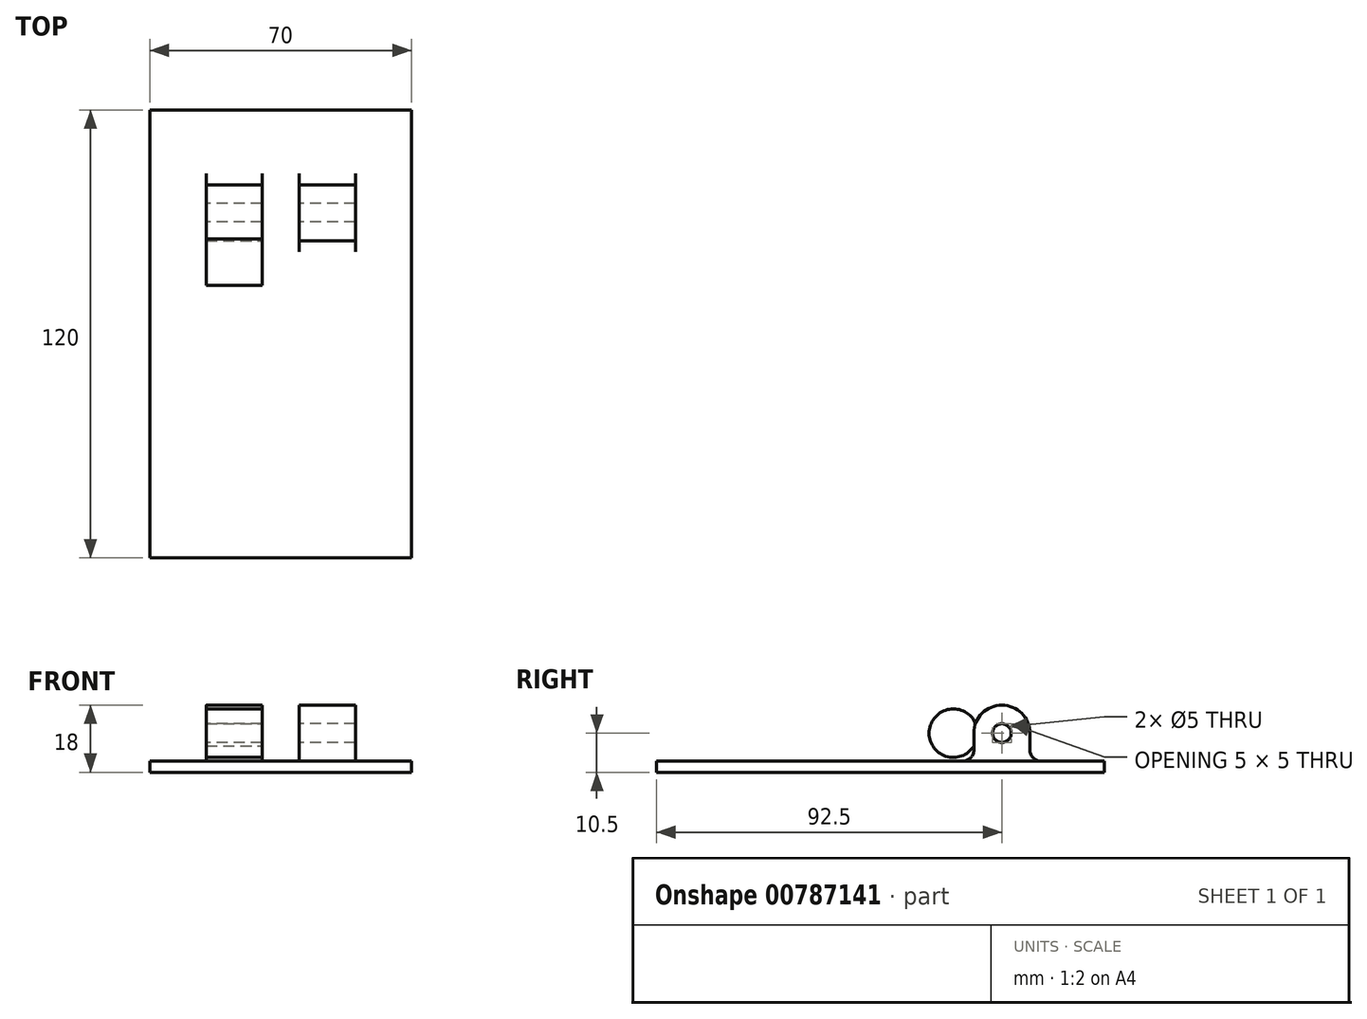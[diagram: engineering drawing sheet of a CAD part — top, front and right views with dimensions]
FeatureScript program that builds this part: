
annotation { "Feature Type Name" : "Feature", "Feature Type Description" : "" }
export const myFeature = defineFeature(function(context is Context, id is Id, definition is map)
    precondition{}
    {
        {
            var Q0;
            Q0=qCreatedBy(makeId("Right.planeOp"),FACE);
            var sketch = newSketch(context, id + "F0", { "sketchPlane" : qUnion([Q0])});
            skLineSegment(sketch, "E0.bottom", {"start": v(0, 0) * mm, "end": v(120, 0) * mm});
            skLineSegment(sketch, "E0.top", {"start": v(0, -3) * mm, "end": v(120, -3) * mm});
            skLineSegment(sketch, "E0.left", {"start": v(0, 0) * mm, "end": v(0, -3) * mm});
            skLineSegment(sketch, "E0.right", {"start": v(120, 0) * mm, "end": v(120, -3) * mm});
            skLineSegment(sketch, "E1.bottom", {"start": v(85, 0) * mm, "end": v(100, 0) * mm});
            skLineSegment(sketch, "E1.top", {"start": v(85, 15) * mm, "end": v(100, 15) * mm});
            skLineSegment(sketch, "E1.left", {"start": v(85, 0) * mm, "end": v(85, 15) * mm});
            skLineSegment(sketch, "E1.right", {"start": v(100, 0) * mm, "end": v(100, 15) * mm});
            skLineSegment(sketch, "E2", {"start": v(85, 15) * mm, "end": v(100, 0) * mm, "construction": true});
            skPoint(sketch, "E3", {"position": v(92.5, 7.5) * mm});
            skSolve(sketch);
        }
        {
            var Q0;
            Q0=makeQuery(id+"F0.imprint","IMPRINT",FACE,{"disambiguationData":[TD([[makeQuery(id+"F0.imprint","IMPRINT",EDGE,{"derivedFrom":sQuery(id+"F0.wireOp",EDGE,"E1.top")}),-1.0]])]});
            var Q1;
            Q1=makeQuery(id+"F0.imprint","IMPRINT",FACE,{"disambiguationData":[TD([[makeQuery(id+"F0.imprint","IMPRINT",EDGE,{"derivedFrom":sQuery(id+"F0.wireOp",EDGE,"E0.top")}),1.0]])]});
            extrude(context, id + "F1", {"entities" : qUnion([Q0, Q1]), "depth" : 70 * mm, "offsetDistance" : 25 * mm});
        }
        {
            var Q0;
            Q0=sQuery(id+"F0.wireOp",VERTEX,"E3");
            var Q1;
            Q1=makeQuery(id+"F1.opExtrude","SWEPT_BODY",BODY,{"disambiguationData":[OSD([sQuery(id+"F0.wireOp",EDGE,"E0.bottom"),sQuery(id+"F0.wireOp",EDGE,"E0.top"),sQuery(id+"F0.wireOp",EDGE,"E0.left"),sQuery(id+"F0.wireOp",EDGE,"E0.right"),sQuery(id+"F0.wireOp",EDGE,"E1.top"),sQuery(id+"F0.wireOp",EDGE,"E1.left"),sQuery(id+"F0.wireOp",EDGE,"E1.right")])]});
            hole(context, id + "F2", {"style" : HoleStyle.SIMPLE, "endStyle" : HoleEndStyle.THROUGH, "oppositeDirection" : true, "holeDiameter" : 5 * mm, "majorDiameter" : 5 * mm, "isTappedThrough" : true, "tappedDepth" : 12 * mm, "tapClearance" : 3, "locations" : qUnion([Q0]), "scope" : qUnion([Q1])});
        }
        {
            var Q0;
            Q0=makeQuery(id+"F1.opExtrude","SWEPT_FACE",FACE,{"disambiguationData":[OSD([sQuery(id+"F0.wireOp",EDGE,"E1.right")])]});
            var sketch = newSketch(context, id + "F3", { "sketchPlane" : qUnion([Q0])});
            skLineSegment(sketch, "E4.bottom", {"start": v(-70, 15) * mm, "end": v(-55, 15) * mm});
            skLineSegment(sketch, "E4.top", {"start": v(-70, 0) * mm, "end": v(-55, 0) * mm});
            skLineSegment(sketch, "E4.left", {"start": v(-70, 15) * mm, "end": v(-70, 0) * mm});
            skLineSegment(sketch, "E4.right", {"start": v(-55, 15) * mm, "end": v(-55, 0) * mm});
            skLineSegment(sketch, "E5.bottom", {"start": v(0, 15) * mm, "end": v(-15, 15) * mm});
            skLineSegment(sketch, "E5.top", {"start": v(0, 0) * mm, "end": v(-15, 0) * mm});
            skLineSegment(sketch, "E5.left", {"start": v(0, 15) * mm, "end": v(0, 0) * mm});
            skLineSegment(sketch, "E5.right", {"start": v(-15, 15) * mm, "end": v(-15, 0) * mm});
            skLineSegment(sketch, "E6", {"start": v(-35, 15) * mm, "end": v(-35, 0) * mm, "construction": true});
            skLineSegment(sketch, "E7.bottom", {"start": v(-30, 0) * mm, "end": v(-40, 0) * mm});
            skLineSegment(sketch, "E7.top", {"start": v(-30, 15) * mm, "end": v(-40, 15) * mm});
            skLineSegment(sketch, "E7.left", {"start": v(-30, 0) * mm, "end": v(-30, 15) * mm});
            skLineSegment(sketch, "E7.right", {"start": v(-40, 0) * mm, "end": v(-40, 15) * mm});
            skPoint(sketch, "E7.middle", {"position": v(-35, 7.5) * mm});
            skSolve(sketch);
        }
        {
            var Q0;
            Q0=makeQuery(id+"F1.opExtrude","SWEPT_EDGE",EDGE,{"disambiguationData":[OSD([sQuery(id+"F0.wireOp",EDGE,"E1.top"),sQuery(id+"F0.wireOp",EDGE,"E1.left")])]});
            var Q1;
            Q1=makeQuery(id+"F1.opExtrude","SWEPT_EDGE",EDGE,{"disambiguationData":[OSD([sQuery(id+"F0.wireOp",EDGE,"E1.top"),sQuery(id+"F0.wireOp",EDGE,"E1.right")])]});
            fillet(context, id + "F4", {"entities" : qUnion([Q0, Q1]), "radius" : 7.5 * mm, "tangentPropagation" : true, "allowEdgeOverflow" : false});
        }
        {
            var Q0;
            Q0=makeQuery(id+"F3.imprint","IMPRINT",FACE,{"disambiguationData":[TD([[makeQuery(id+"F3.imprint","IMPRINT",EDGE,{"derivedFrom":sQuery(id+"F3.wireOp",EDGE,"E4.bottom")}),-1.0]])]});
            var Q1;
            Q1=makeQuery(id+"F3.imprint","IMPRINT",FACE,{"disambiguationData":[TD([[makeQuery(id+"F3.imprint","IMPRINT",EDGE,{"derivedFrom":sQuery(id+"F3.wireOp",EDGE,"E5.bottom")}),-1.0]])]});
            var Q2;
            Q2=makeQuery(id+"F3.imprint","IMPRINT",FACE,{"disambiguationData":[TD([[makeQuery(id+"F3.imprint","IMPRINT",EDGE,{"derivedFrom":sQuery(id+"F3.wireOp",EDGE,"E7.bottom")}),1.0]])]});
            var Q3;
            Q3=makeQuery(id+"F1.opExtrude","SWEPT_FACE",FACE,{"disambiguationData":[OSD([sQuery(id+"F0.wireOp",EDGE,"E1.left")])]});
            extrude(context, id + "F5", {"entities" : qUnion([Q0, Q1, Q2]), "operationType" : NewBodyOperationType.REMOVE, "endBound" : BoundingType.UP_TO_SURFACE, "oppositeDirection" : true, "depth" : 25 * mm, "endBoundEntityFace" : qUnion([Q3]), "offsetDistance" : 25 * mm});
        }
        {
            var Q0;
            {var subQ1=sQuery(id+"F0.wireOp",EDGE,"E1.left");var subQ3=sQuery(id+"F0.wireOp",EDGE,"E0.bottom");var subQ8=makeQuery(id+"F1.opExtrude","SWEPT_EDGE",EDGE,{"disambiguationData":[OSD([subQ3,subQ1])]});Q0=qUnion([makeQuery(id+"F5.boolean.opBoolean","SPLIT",EDGE,{"disambiguationData":[TD([makeQuery(id+"F5.opExtrude","SWEPT_FACE",FACE,{"disambiguationData":[OSD([sQuery(id+"F3.wireOp",EDGE,"E4.right")])]})])],"derivedFrom":subQ8}),makeQuery(id+"F5.boolean.opBoolean","SPLIT",EDGE,{"disambiguationData":[TD([makeQuery(id+"F5.opExtrude","SWEPT_FACE",FACE,{"disambiguationData":[OSD([sQuery(id+"F3.wireOp",EDGE,"E5.right")])]})])],"derivedFrom":subQ8})]);}
            var Q1;
            {var subQ1=sQuery(id+"F0.wireOp",EDGE,"E1.right");var subQ3=sQuery(id+"F0.wireOp",EDGE,"E0.bottom");var subQ8=makeQuery(id+"F1.opExtrude","SWEPT_EDGE",EDGE,{"disambiguationData":[OSD([subQ3,subQ1])]});Q1=qUnion([makeQuery(id+"F5.boolean.opBoolean","SPLIT",EDGE,{"disambiguationData":[TD([makeQuery(id+"F5.opExtrude","SWEPT_FACE",FACE,{"disambiguationData":[OSD([sQuery(id+"F3.wireOp",EDGE,"E5.right")])]})])],"derivedFrom":subQ8}),makeQuery(id+"F5.boolean.opBoolean","SPLIT",EDGE,{"disambiguationData":[TD([makeQuery(id+"F5.opExtrude","SWEPT_FACE",FACE,{"disambiguationData":[OSD([sQuery(id+"F3.wireOp",EDGE,"E4.right")])]})])],"derivedFrom":subQ8})]);}
            fillet(context, id + "F6", {"entities" : qUnion([Q0, Q1]), "radius" : 3 * mm, "tangentPropagation" : true, "allowEdgeOverflow" : false});
        }
        {
            var Q0;
            Q0=makeQuery(id+"F5.boolean.opBoolean","COPY",FACE,{"derivedFrom":makeQuery(id+"F5.opExtrude","SWEPT_FACE",FACE,{"disambiguationData":[OSD([sQuery(id+"F3.wireOp",EDGE,"E7.left")])]})});
            var sketch = newSketch(context, id + "F7", { "sketchPlane" : qUnion([Q0])});
            skCircle(sketch, "E8", {"center": v(92.5, 7.5) * mm, "radius": 6.5 * mm});
            skCircle(sketch, "E9", {"center": v(79.5, 7.5) * mm, "radius": 6.5 * mm});
            skLineSegment(sketch, "E10", {"start": v(92.5, 0) * mm, "end": v(92.5, 1) * mm, "construction": true});
            skLineSegment(sketch, "E11", {"start": v(92.5, 1) * mm, "end": v(79.5, 1) * mm, "construction": true});
            skSolve(sketch);
        }
        {
            var Q0;
            {var subQ0=sQuery(id+"F7.wireOp",EDGE,"E9");var subQ1=sQuery(id+"F3.wireOp",EDGE,"E7.left");var subQ2=makeQuery(id+"F5.boolean.opBoolean","COPY",EDGE,{"derivedFrom":makeQuery(id+"F5.opExtrude","CAP_EDGE",EDGE,{"disambiguationData":[OSD([subQ1])],"isStart":false})});var subQ3=makeQuery(id+"F7.imprint","INTERSECT",VERTEX,{"derivedFrom":[subQ2,subQ0]});Q0=makeQuery(id+"F7.imprint","IMPRINT",FACE,{"disambiguationData":[TD([[makeQuery(id+"F7.imprint","IMPRINT",EDGE,{"disambiguationData":[TD([[subQ3,1.0]])],"derivedFrom":subQ0}),1.0]])]});}
            var Q1;
            {var subQ0=sQuery(id+"F7.wireOp",EDGE,"E9");var subQ1=makeQuery(id+"F7.imprint","INTERSECT",VERTEX,{"derivedFrom":[sQuery(id+"F7.wireOp",EDGE,"E8"),subQ0]});Q1=makeQuery(id+"F7.imprint","IMPRINT",FACE,{"disambiguationData":[TD([[makeQuery(id+"F7.imprint","IMPRINT",EDGE,{"disambiguationData":[TD([[subQ1,1.0]])],"derivedFrom":subQ0}),1.0]])]});}
            var Q2;
            Q2=makeQuery(id+"F5.boolean.opBoolean","COPY",FACE,{"derivedFrom":makeQuery(id+"F5.opExtrude","SWEPT_FACE",FACE,{"disambiguationData":[OSD([sQuery(id+"F3.wireOp",EDGE,"E5.right")])]})});
            extrude(context, id + "F8", {"entities" : qUnion([Q0, Q1]), "operationType" : NewBodyOperationType.ADD, "endBound" : BoundingType.UP_TO_SURFACE, "oppositeDirection" : true, "depth" : 25 * mm, "endBoundEntityFace" : qUnion([Q2]), "offsetDistance" : 25 * mm});
        }
    });
